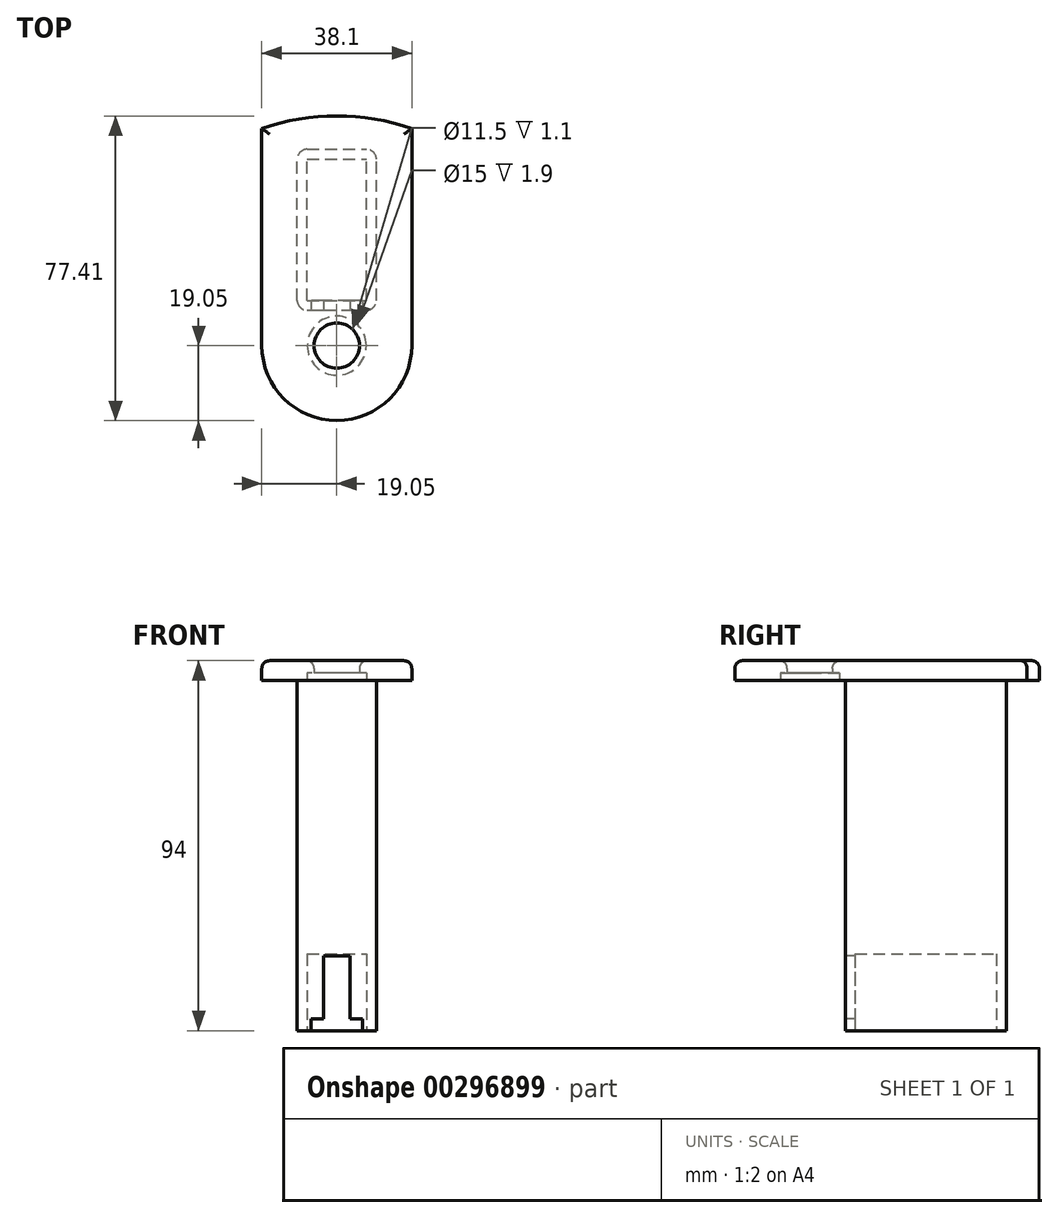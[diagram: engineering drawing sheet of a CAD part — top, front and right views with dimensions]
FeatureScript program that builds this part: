
annotation { "Feature Type Name" : "Feature", "Feature Type Description" : "" }
export const myFeature = defineFeature(function(context is Context, id is Id, definition is map)
    precondition{}
    {
        {
            var Q0;
            Q0=qCreatedBy(makeId("Top.planeOp"),FACE);
            var sketch = newSketch(context, id + "F0", { "sketchPlane" : qUnion([Q0])});
            skLineSegment(sketch, "E0.bottom", {"start": v(0, 0) * mm, "end": v(10.05, 0) * mm});
            skLineSegment(sketch, "E0.top", {"start": v(0, 40.9) * mm, "end": v(10.05, 40.9) * mm});
            skLineSegment(sketch, "E0.left", {"start": v(0, 0) * mm, "end": v(0, 40.9) * mm});
            skLineSegment(sketch, "E0.right", {"start": v(10.05, 0) * mm, "end": v(10.05, 40.9) * mm});
            skPoint(sketch, "E1", {"position": v(0, -9) * mm});
            skCircle(sketch, "E2", {"center": v(0, -9) * mm, "radius": 58.36 * mm});
            skCircle(sketch, "E3", {"center": v(0, -9) * mm, "radius": 5.75 * mm});
            skLineSegment(sketch, "E4.bottom", {"start": v(-10.05, 0) * mm, "end": v(0, 0) * mm});
            skLineSegment(sketch, "E4.top", {"start": v(-10.05, 40.9) * mm, "end": v(0, 40.9) * mm});
            skLineSegment(sketch, "E4.left", {"start": v(-10.05, 0) * mm, "end": v(-10.05, 40.9) * mm});
            skSolve(sketch);
        }
        {
            var Q0;
            Q0=makeQuery(id+"F0.imprint","IMPRINT",FACE,{"disambiguationData":[TD([[makeQuery(id+"F0.imprint","IMPRINT",EDGE,{"derivedFrom":sQuery(id+"F0.wireOp",EDGE,"E0.bottom")}),1.0]])]});
            var Q1;
            Q1=makeQuery(id+"F0.imprint","IMPRINT",FACE,{"disambiguationData":[TD([[makeQuery(id+"F0.imprint","IMPRINT",EDGE,{"derivedFrom":sQuery(id+"F0.wireOp",EDGE,"E4.bottom")}),1.0]])]});
            var Q2;
            Q2=makeQuery(id+"F0.imprint","IMPRINT",FACE,{"disambiguationData":[TD([[makeQuery(id+"F0.imprint","IMPRINT",EDGE,{"derivedFrom":sQuery(id+"F0.wireOp",EDGE,"qfhPdZtq-EUDK-GF1x-wlXW-LFGvO33lR6iL")}),1.0]])]});
            var Q3;
            Q3=makeQuery(id+"F0.imprint","IMPRINT",FACE,{"disambiguationData":[TD([[makeQuery(id+"F0.imprint","IMPRINT",EDGE,{"derivedFrom":sQuery(id+"F0.wireOp",EDGE,"E0.bottom")}),-1.0]])]});
            extrude(context, id + "F1", {"entities" : qUnion([Q0, Q1, Q2, Q3]), "depth" : 5 * mm});
        }
        {
            var Q0;
            Q0=makeQuery(id+"F0.imprint","IMPRINT",FACE,{"disambiguationData":[TD([[makeQuery(id+"F0.imprint","IMPRINT",EDGE,{"derivedFrom":sQuery(id+"F0.wireOp",EDGE,"E0.bottom")}),1.0]])]});
            var Q1;
            Q1=makeQuery(id+"F0.imprint","IMPRINT",FACE,{"disambiguationData":[TD([[makeQuery(id+"F0.imprint","IMPRINT",EDGE,{"derivedFrom":sQuery(id+"F0.wireOp",EDGE,"E4.bottom")}),1.0]])]});
            extrude(context, id + "F2", {"entities" : qUnion([Q0, Q1]), "operationType" : NewBodyOperationType.ADD, "oppositeDirection" : true, "depth" : 89 * mm});
        }
        {
            var Q0;
            Q0=makeQuery(id+"F2.opExtrude","CAP_FACE",FACE,{"disambiguationData":[OSD([sQuery(id+"F0.wireOp",EDGE,"E0.bottom"),sQuery(id+"F0.wireOp",EDGE,"E0.top"),sQuery(id+"F0.wireOp",EDGE,"E0.right"),sQuery(id+"F0.wireOp",EDGE,"E4.bottom"),sQuery(id+"F0.wireOp",EDGE,"E4.top"),sQuery(id+"F0.wireOp",EDGE,"E4.left")])],"isStart":false});
            cPlane(context, id + "F3", {"entities" : qUnion([Q0]), "cplaneType" : CPlaneType.OFFSET, "offset" : 0 * mm, "width" : 150 * mm, "height" : 150 * mm});
        }
        {
            var Q0;
            Q0=qCreatedBy(id+"F3.planeOp",FACE);
            var sketch = newSketch(context, id + "F4", { "sketchPlane" : qUnion([Q0])});
            skLineSegment(sketch, "E5.bottom", {"start": v(-7.55, -2.5) * mm, "end": v(7.55, -2.5) * mm});
            skLineSegment(sketch, "E5.top", {"start": v(-7.55, -38.4) * mm, "end": v(7.55, -38.4) * mm});
            skLineSegment(sketch, "E5.left", {"start": v(-7.55, -2.5) * mm, "end": v(-7.55, -38.4) * mm});
            skLineSegment(sketch, "E5.right", {"start": v(7.55, -2.5) * mm, "end": v(7.55, -38.4) * mm});
            skSolve(sketch);
        }
        {
            var Q0;
            Q0 = qSketchRegion(id + "F4", true);
            extrude(context, id + "F5", {"entities" : qUnion([Q0]), "operationType" : NewBodyOperationType.REMOVE, "oppositeDirection" : true, "depth" : 19.5 * mm});
        }
        {
            var Q0;
            Q0=makeQuery(id+"F2.opExtrude","SWEPT_FACE",FACE,{"disambiguationData":[OSD([sQuery(id+"F0.wireOp",EDGE,"E0.bottom"),sQuery(id+"F0.wireOp",EDGE,"E4.bottom")])]});
            cPlane(context, id + "F6", {"entities" : qUnion([Q0]), "cplaneType" : CPlaneType.OFFSET, "offset" : 0 * mm, "width" : 150 * mm, "height" : 150 * mm});
        }
        {
            var Q0;
            Q0=qCreatedBy(id+"F6.planeOp",FACE);
            var sketch = newSketch(context, id + "F7", { "sketchPlane" : qUnion([Q0])});
            skLineSegment(sketch, "E6.top", {"start": v(0, -70) * mm, "end": v(-3.37, -70) * mm});
            skLineSegment(sketch, "E6.right", {"start": v(-3.37, -86) * mm, "end": v(-3.37, -70) * mm});
            skLineSegment(sketch, "E7.top", {"start": v(0, -70) * mm, "end": v(3.38, -70) * mm});
            skLineSegment(sketch, "E7.right", {"start": v(3.38, -86) * mm, "end": v(3.38, -70) * mm});
            skLineSegment(sketch, "E8", {"start": v(3.38, -89) * mm, "end": v(-3.37, -89) * mm});
            skLineSegment(sketch, "E9", {"start": v(0, 0) * mm, "end": v(0, -70) * mm, "construction": true});
            skLineSegment(sketch, "E10", {"start": v(3.38, -86) * mm, "end": v(6.5, -86) * mm});
            skLineSegment(sketch, "E11", {"start": v(6.5, -86) * mm, "end": v(6.5, -89) * mm});
            skLineSegment(sketch, "E12", {"start": v(6.5, -89) * mm, "end": v(-6.5, -89) * mm});
            skPoint(sketch, "E12.endSnap0", {"position": v(0, -89) * mm});
            skLineSegment(sketch, "E13", {"start": v(-6.5, -89) * mm, "end": v(-6.5, -86) * mm});
            skLineSegment(sketch, "E14", {"start": v(-6.5, -86) * mm, "end": v(-3.38, -86) * mm});
            skLineSegment(sketch, "E15", {"start": v(-3.38, -86) * mm, "end": v(3.38, -86) * mm, "construction": true});
            skSolve(sketch);
        }
        {
            var Q0;
            Q0 = qSketchRegion(id + "F7", true);
            extrude(context, id + "F8", {"entities" : qUnion([Q0]), "operationType" : NewBodyOperationType.REMOVE, "oppositeDirection" : true, "depth" : 25 * mm});
        }
        {
            var Q0;
            Q0=makeQuery(id+"F0.imprint","IMPRINT",FACE,{"disambiguationData":[TD([[makeQuery(id+"F0.imprint","IMPRINT",EDGE,{"derivedFrom":sQuery(id+"F0.wireOp",EDGE,"E0.bottom")}),-1.0]])]});
            var sketch = newSketch(context, id + "F9", { "sketchPlane" : qUnion([Q0])});
            skCircle(sketch, "E16", {"center": v(0, -9) * mm, "radius": 7.5 * mm});
            skSolve(sketch);
        }
        {
            var Q0;
            Q0 = qSketchRegion(id + "F9", true);
            extrude(context, id + "F10", {"entities" : qUnion([Q0]), "operationType" : NewBodyOperationType.REMOVE, "depth" : 1.9 * mm});
        }
        {
            var Q0;
            Q0=makeQuery(id+"F0.imprint","IMPRINT",FACE,{"disambiguationData":[TD([[makeQuery(id+"F0.imprint","IMPRINT",EDGE,{"derivedFrom":sQuery(id+"F0.wireOp",EDGE,"E0.bottom")}),-1.0]])]});
            var sketch = newSketch(context, id + "F11", { "sketchPlane" : qUnion([Q0])});
            skArc(sketch, "E17", {"start": v(-19.05, -9) * mm, "mid": v(0, -28.05) * mm, "end": v(19.05, -9) * mm});
            skLineSegment(sketch, "E18", {"start": v(19.05, -9) * mm, "end": v(19.05, 46.17) * mm});
            skLineSegment(sketch, "E19", {"start": v(-19.05, -9) * mm, "end": v(-19.05, 46.17) * mm});
            skArc(sketch, "E20.0", {"start": v(-19.05, 46.17) * mm, "mid": v(0, -67.36) * mm, "end": v(19.05, 46.17) * mm});
            skSolve(sketch);
        }
        {
            var Q0;
            Q0 = qSketchRegion(id + "F11", true);
            extrude(context, id + "F12", {"entities" : qUnion([Q0]), "operationType" : NewBodyOperationType.REMOVE, "endBound" : BoundingType.THROUGH_ALL, "depth" : 25 * mm});
        }
        {
            var Q0;
            Q0=makeQuery(id+"F2.opExtrude","CAP_EDGE",EDGE,{"disambiguationData":[OSD([sQuery(id+"F0.wireOp",EDGE,"E4.left")])],"isStart":true});
            var Q1;
            Q1=makeQuery(id+"F2.opExtrude","CAP_EDGE",EDGE,{"disambiguationData":[OSD([sQuery(id+"F0.wireOp",EDGE,"E0.bottom"),sQuery(id+"F0.wireOp",EDGE,"E4.bottom")])],"isStart":true});
            var Q2;
            Q2=makeQuery(id+"F2.opExtrude","CAP_EDGE",EDGE,{"disambiguationData":[OSD([sQuery(id+"F0.wireOp",EDGE,"E0.right")])],"isStart":true});
            var Q3;
            Q3=makeQuery(id+"F2.opExtrude","CAP_EDGE",EDGE,{"disambiguationData":[OSD([sQuery(id+"F0.wireOp",EDGE,"E0.top"),sQuery(id+"F0.wireOp",EDGE,"E4.top")])],"isStart":true});
            var Q4;
            Q4=makeQuery(id+"F2.opExtrude","SWEPT_EDGE",EDGE,{"disambiguationData":[OSD([sQuery(id+"F0.wireOp",EDGE,"E0.top"),sQuery(id+"F0.wireOp",EDGE,"E0.right")])]});
            var Q5;
            Q5=makeQuery(id+"F2.opExtrude","SWEPT_EDGE",EDGE,{"disambiguationData":[OSD([sQuery(id+"F0.wireOp",EDGE,"E4.top"),sQuery(id+"F0.wireOp",EDGE,"E4.left")])]});
            var Q6;
            Q6=makeQuery(id+"F2.opExtrude","SWEPT_EDGE",EDGE,{"disambiguationData":[OSD([sQuery(id+"F0.wireOp",EDGE,"E0.bottom"),sQuery(id+"F0.wireOp",EDGE,"E0.right")])]});
            var Q7;
            Q7=makeQuery(id+"F2.opExtrude","SWEPT_EDGE",EDGE,{"disambiguationData":[OSD([sQuery(id+"F0.wireOp",EDGE,"E4.bottom"),sQuery(id+"F0.wireOp",EDGE,"E4.left")])]});
            fillet(context, id + "F13", {"entities" : qUnion([Q0, Q1, Q2, Q3, Q4, Q5, Q6, Q7]), "radius" : 2.5 * mm, "tangentPropagation" : true, "allowEdgeOverflow" : false});
        }
        {
            var Q0;
            Q0=makeQuery(id+"F1.opExtrude","CAP_FACE",FACE,{"disambiguationData":[OSD([sQuery(id+"F0.wireOp",EDGE,"E2"),sQuery(id+"F0.wireOp",EDGE,"E3")])],"isStart":false});
            var Q1;
            Q1=makeQuery(id+"F1.opExtrude","CAP_EDGE",EDGE,{"disambiguationData":[OSD([sQuery(id+"F0.wireOp",EDGE,"E3")])],"isStart":false});
            fillet(context, id + "F14", {"entities" : qUnion([Q0, Q1]), "radius" : 2 * mm, "tangentPropagation" : true, "allowEdgeOverflow" : false});
        }
        {
            var Q0;
            Q0 = qSketchRegion(id + "F7", true);
            extrude(context, id + "F15", {"entities" : qUnion([Q0]), "operationType" : NewBodyOperationType.REMOVE, "oppositeDirection" : true, "depth" : 25 * mm});
        }
    });
